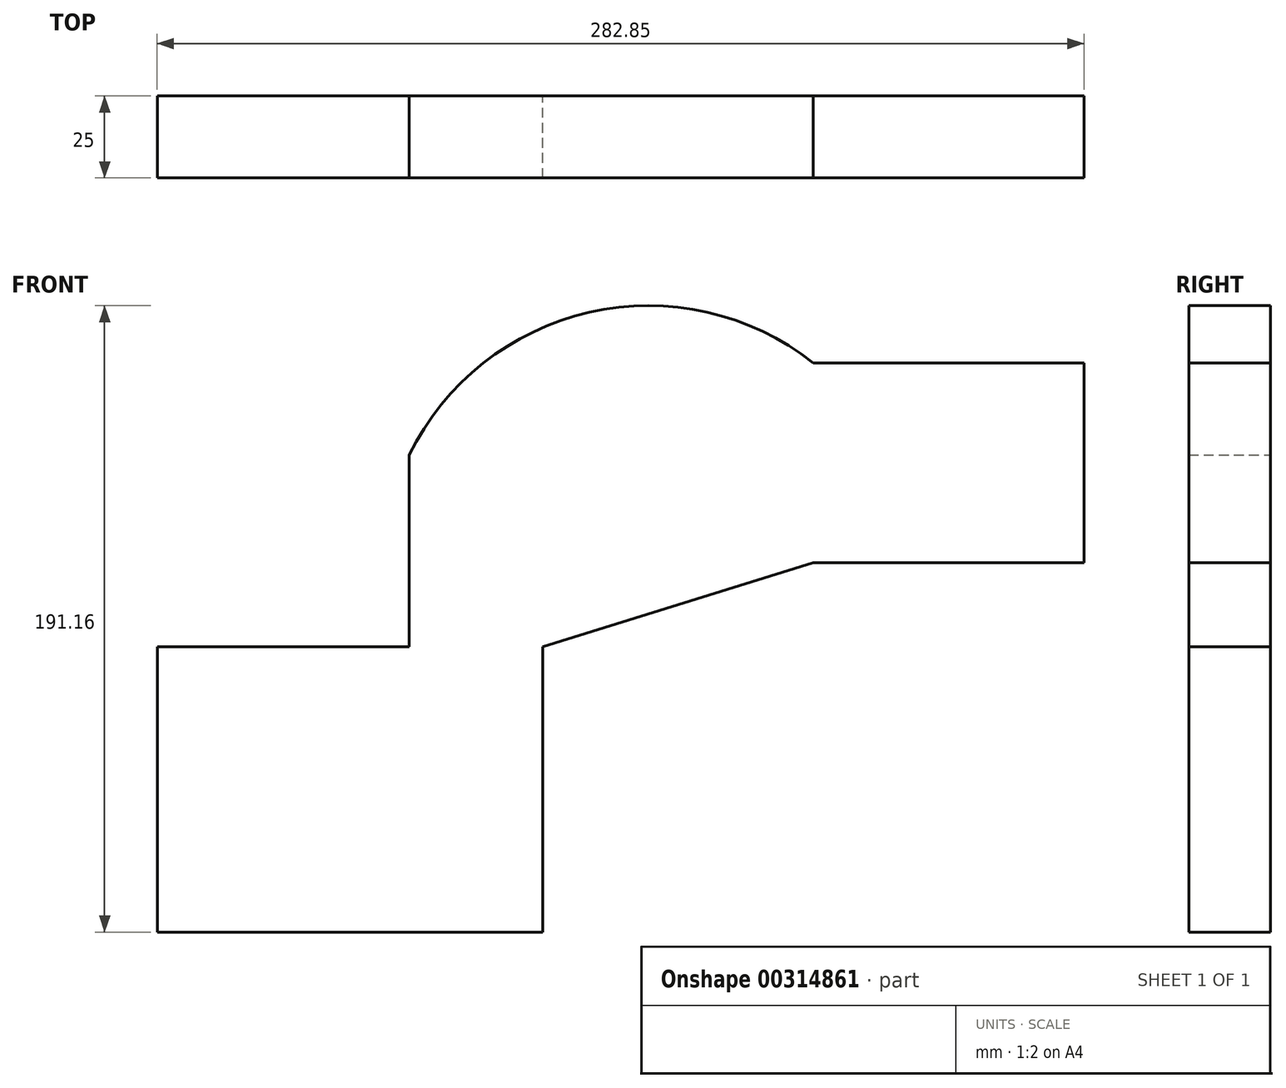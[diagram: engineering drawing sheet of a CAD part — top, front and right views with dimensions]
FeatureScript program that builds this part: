
annotation { "Feature Type Name" : "Feature", "Feature Type Description" : "" }
export const myFeature = defineFeature(function(context is Context, id is Id, definition is map)
    precondition{}
    {
        {
            var Q0;
            Q0=qCreatedBy(makeId("Front.planeOp"),FACE);
            var sketch = newSketch(context, id + "F0", { "sketchPlane" : qUnion([Q0])});
            skLineSegment(sketch, "E0.bottom", {"start": v(-70.71, -66.23) * mm, "end": v(-188.38, -66.23) * mm});
            skLineSegment(sketch, "E0.top", {"start": v(-70.71, 20.86) * mm, "end": v(-188.38, 20.86) * mm});
            skLineSegment(sketch, "E0.left", {"start": v(-70.71, -66.23) * mm, "end": v(-70.71, 20.86) * mm});
            skLineSegment(sketch, "E0.right", {"start": v(-188.38, -66.23) * mm, "end": v(-188.38, 20.86) * mm});
            skPoint(sketch, "E0.middle", {"position": v(-129.54, -22.69) * mm});
            skLineSegment(sketch, "E1.bottom", {"start": v(94.47, 46.5) * mm, "end": v(11.88, 46.5) * mm});
            skLineSegment(sketch, "E1.top", {"start": v(94.47, 107.52) * mm, "end": v(11.88, 107.52) * mm});
            skLineSegment(sketch, "E1.left", {"start": v(94.47, 46.5) * mm, "end": v(94.47, 107.52) * mm});
            skLineSegment(sketch, "E1.right", {"start": v(11.88, 46.5) * mm, "end": v(11.88, 107.52) * mm});
            skPoint(sketch, "E1.middle", {"position": v(53.18, 77.01) * mm});
            skLineSegment(sketch, "E2", {"start": v(-111.44, 20.86) * mm, "end": v(-111.44, 79.43) * mm});
            skArc(sketch, "E3", {"start": v(11.88, 107.52) * mm, "mid": v(-56.48, 122.9) * mm, "end": v(-111.44, 79.43) * mm});
            skLineSegment(sketch, "E4", {"start": v(-70.71, 20.86) * mm, "end": v(11.88, 46.5) * mm});
            skSolve(sketch);
        }
        {
            var Q0;
            Q0=makeQuery(id+"F0.imprint","IMPRINT",FACE,{"disambiguationData":[TD([[makeQuery(id+"F0.imprint","IMPRINT",EDGE,{"derivedFrom":sQuery(id+"F0.wireOp",EDGE,"E0.bottom")}),-1.0]])]});
            var Q1;
            Q1=makeQuery(id+"F0.imprint","IMPRINT",FACE,{"disambiguationData":[TD([[makeQuery(id+"F0.imprint","IMPRINT",EDGE,{"derivedFrom":sQuery(id+"F0.wireOp",EDGE,"E1.bottom")}),-1.0]])]});
            var Q2;
            Q2=makeQuery(id+"F0.imprint","IMPRINT",FACE,{"disambiguationData":[TD([[makeQuery(id+"F0.imprint","IMPRINT",EDGE,{"derivedFrom":sQuery(id+"F0.wireOp",EDGE,"E1.right")}),1.0]])]});
            extrude(context, id + "F1", {"entities" : qUnion([Q0, Q1, Q2]), "endBound" : BoundingType.SYMMETRIC, "depth" : 25 * mm});
        }
    });
